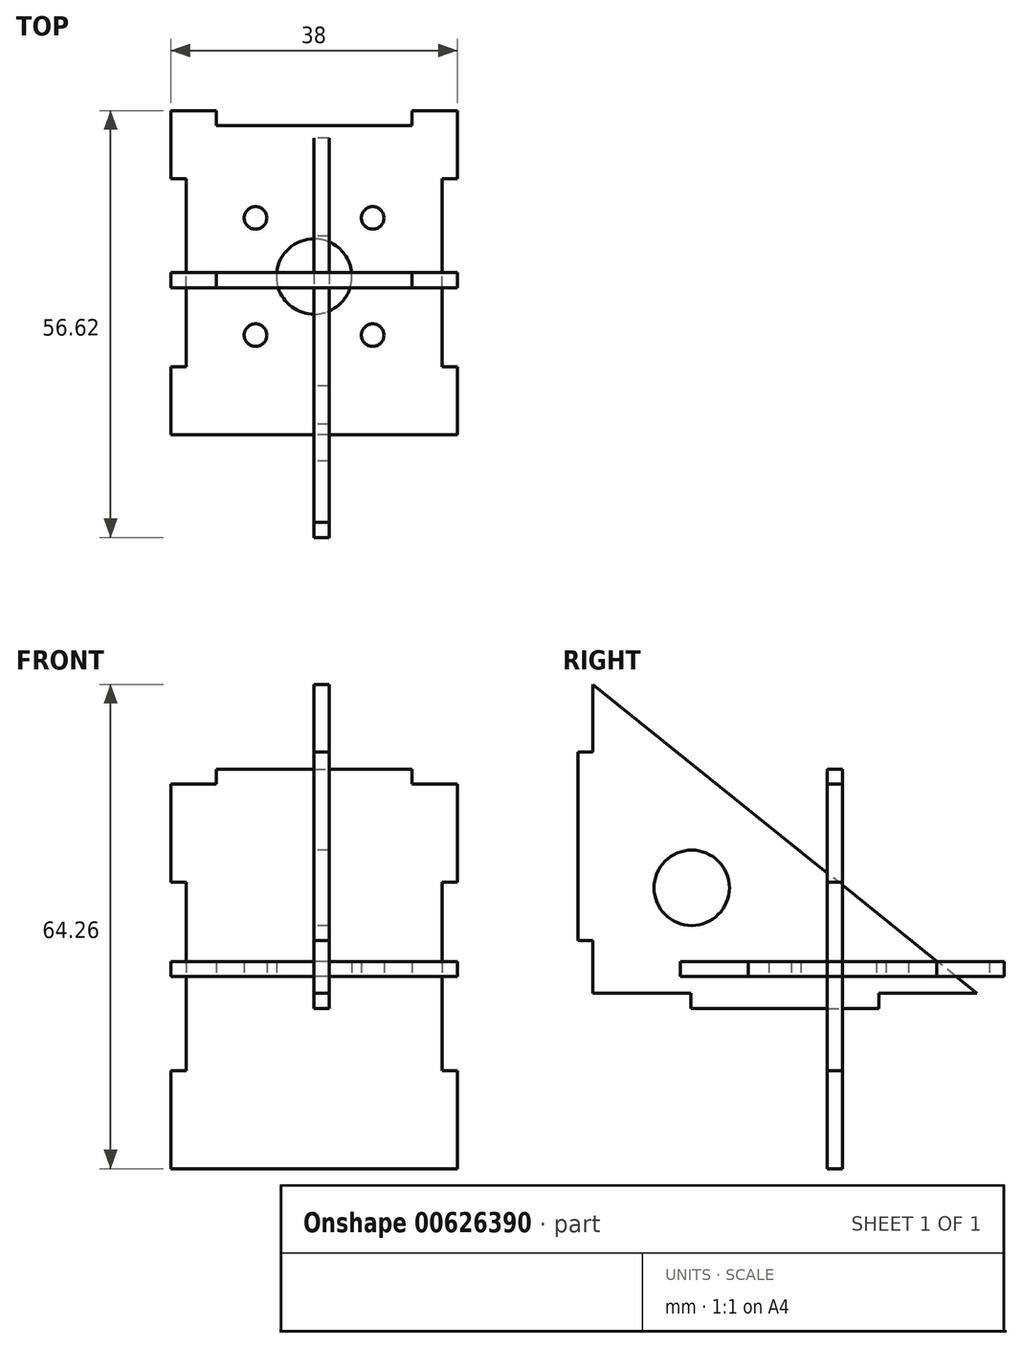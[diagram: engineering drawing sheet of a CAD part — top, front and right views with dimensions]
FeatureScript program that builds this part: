
annotation { "Feature Type Name" : "Feature", "Feature Type Description" : "" }
export const myFeature = defineFeature(function(context is Context, id is Id, definition is map)
    precondition{}
    {
        {
            var Q0;
            Q0=qCreatedBy(makeId("Front.planeOp"),FACE);
            var sketch = newSketch(context, id + "F0", { "sketchPlane" : qUnion([Q0])});
            skLineSegment(sketch, "E0.bottom", {"start": v(19, 25.5) * mm, "end": v(13, 25.5) * mm});
            skLineSegment(sketch, "E0.top", {"start": v(19, -25.5) * mm, "end": v(-19, -25.5) * mm});
            skLineSegment(sketch, "E0.left", {"start": v(19, 25.5) * mm, "end": v(19, 12.5) * mm});
            skLineSegment(sketch, "E0.right", {"start": v(-19, 25.5) * mm, "end": v(-19, 12.5) * mm});
            skPoint(sketch, "E0.middle", {"position": v(0, 0) * mm});
            skLineSegment(sketch, "E1", {"start": v(0, 28.55) * mm, "end": v(0, -30.47) * mm, "construction": true});
            skLineSegment(sketch, "E2.top", {"start": v(-13, 27.5) * mm, "end": v(13, 27.5) * mm});
            skLineSegment(sketch, "E2.left", {"start": v(-13, 25.5) * mm, "end": v(-13, 27.5) * mm});
            skLineSegment(sketch, "E2.right", {"start": v(13, 25.5) * mm, "end": v(13, 27.5) * mm});
            skLineSegment(sketch, "E3.bottom", {"start": v(-19, 12.5) * mm, "end": v(-17, 12.5) * mm});
            skLineSegment(sketch, "E3.top", {"start": v(-19, -12.5) * mm, "end": v(-17, -12.5) * mm});
            skLineSegment(sketch, "E3.right", {"start": v(-17, 12.5) * mm, "end": v(-17, -12.5) * mm});
            skLineSegment(sketch, "E4.MirrorCS", {"start": v(19, 12.5) * mm, "end": v(17, 12.5) * mm});
            skLineSegment(sketch, "E5.MirrorCS", {"start": v(17, 12.5) * mm, "end": v(17, -12.5) * mm});
            skLineSegment(sketch, "E6.MirrorCS", {"start": v(19, -12.5) * mm, "end": v(17, -12.5) * mm});
            skLineSegment(sketch, "E7.trimOffspring", {"start": v(-13, 25.5) * mm, "end": v(-19, 25.5) * mm});
            skLineSegment(sketch, "E8.trimOffspring", {"start": v(-19, -12.5) * mm, "end": v(-19, -25.5) * mm});
            skLineSegment(sketch, "E9.trimOffspring", {"start": v(19, -12.5) * mm, "end": v(19, -25.5) * mm});
            skSolve(sketch);
        }
        {
            var Q0;
            Q0=makeQuery(id+"F0.imprint","IMPRINT",FACE,{"disambiguationData":[TD([[makeQuery(id+"F0.imprint","IMPRINT",EDGE,{"derivedFrom":sQuery(id+"F0.wireOp",EDGE,"E0.bottom")}),1.0]])]});
            extrude(context, id + "F1", {"entities" : qUnion([Q0]), "depth" : 2 * mm, "offsetDistance" : 25 * mm});
        }
        {
            var Q0;
            Q0=makeQuery(id+"F1.opExtrude","SWEPT_BODY",BODY,{"disambiguationData":[OSD([sQuery(id+"F0.wireOp",EDGE,"E0.bottom"),sQuery(id+"F0.wireOp",EDGE,"E0.top"),sQuery(id+"F0.wireOp",EDGE,"E0.left"),sQuery(id+"F0.wireOp",EDGE,"E0.right"),sQuery(id+"F0.wireOp",EDGE,"E2.top"),sQuery(id+"F0.wireOp",EDGE,"E2.left"),sQuery(id+"F0.wireOp",EDGE,"E2.right"),sQuery(id+"F0.wireOp",EDGE,"E3.bottom"),sQuery(id+"F0.wireOp",EDGE,"E3.top"),sQuery(id+"F0.wireOp",EDGE,"E3.right"),sQuery(id+"F0.wireOp",EDGE,"E4.MirrorCS"),sQuery(id+"F0.wireOp",EDGE,"E5.MirrorCS"),sQuery(id+"F0.wireOp",EDGE,"E6.MirrorCS"),sQuery(id+"F0.wireOp",EDGE,"E7.trimOffspring"),sQuery(id+"F0.wireOp",EDGE,"E8.trimOffspring"),sQuery(id+"F0.wireOp",EDGE,"E9.trimOffspring")])]});
            transform(context, id + "F2", {"entities" : qUnion([Q0]), "transformType" : TransformType.TRANSLATION_3D, "dx" : 0 * mm, "dy" : 0 * mm, "dz" : 0 * mm, "makeCopy" : true});
        }
        {
            var Q0;
            Q0=makeQuery(id+"F2.opPattern","COPY",BODY,{"derivedFrom":makeQuery(id+"F1.opExtrude","SWEPT_BODY",BODY,{"disambiguationData":[OSD([sQuery(id+"F0.wireOp",EDGE,"E0.bottom"),sQuery(id+"F0.wireOp",EDGE,"E0.top"),sQuery(id+"F0.wireOp",EDGE,"E0.left"),sQuery(id+"F0.wireOp",EDGE,"E0.right"),sQuery(id+"F0.wireOp",EDGE,"E2.top"),sQuery(id+"F0.wireOp",EDGE,"E2.left"),sQuery(id+"F0.wireOp",EDGE,"E2.right"),sQuery(id+"F0.wireOp",EDGE,"E3.bottom"),sQuery(id+"F0.wireOp",EDGE,"E3.top"),sQuery(id+"F0.wireOp",EDGE,"E3.right"),sQuery(id+"F0.wireOp",EDGE,"E4.MirrorCS"),sQuery(id+"F0.wireOp",EDGE,"E5.MirrorCS"),sQuery(id+"F0.wireOp",EDGE,"E6.MirrorCS"),sQuery(id+"F0.wireOp",EDGE,"E7.trimOffspring"),sQuery(id+"F0.wireOp",EDGE,"E8.trimOffspring"),sQuery(id+"F0.wireOp",EDGE,"E9.trimOffspring")])]}),"instanceName":"1"});
            deleteBodies(context, id + "F3", {"entities" : qUnion([Q0])});
        }
        {
            var Q0;
            Q0=makeQuery(id+"F1.opExtrude","SWEPT_BODY",BODY,{"disambiguationData":[OSD([sQuery(id+"F0.wireOp",EDGE,"E0.bottom"),sQuery(id+"F0.wireOp",EDGE,"E0.top"),sQuery(id+"F0.wireOp",EDGE,"E0.left"),sQuery(id+"F0.wireOp",EDGE,"E0.right"),sQuery(id+"F0.wireOp",EDGE,"E2.top"),sQuery(id+"F0.wireOp",EDGE,"E2.left"),sQuery(id+"F0.wireOp",EDGE,"E2.right"),sQuery(id+"F0.wireOp",EDGE,"E3.bottom"),sQuery(id+"F0.wireOp",EDGE,"E3.top"),sQuery(id+"F0.wireOp",EDGE,"E3.right"),sQuery(id+"F0.wireOp",EDGE,"E4.MirrorCS"),sQuery(id+"F0.wireOp",EDGE,"E5.MirrorCS"),sQuery(id+"F0.wireOp",EDGE,"E6.MirrorCS"),sQuery(id+"F0.wireOp",EDGE,"E7.trimOffspring"),sQuery(id+"F0.wireOp",EDGE,"E8.trimOffspring"),sQuery(id+"F0.wireOp",EDGE,"E9.trimOffspring")])]});
            transform(context, id + "F4", {"entities" : qUnion([Q0]), "transformType" : TransformType.TRANSLATION_3D, "dx" : 0 * mm, "dy" : 0 * mm, "dz" : 0 * mm, "makeCopy" : true});
        }
        {
            var Q0;
            Q0=makeQuery(id+"F4.opPattern","COPY",BODY,{"derivedFrom":makeQuery(id+"F1.opExtrude","SWEPT_BODY",BODY,{"disambiguationData":[OSD([sQuery(id+"F0.wireOp",EDGE,"E0.bottom"),sQuery(id+"F0.wireOp",EDGE,"E0.top"),sQuery(id+"F0.wireOp",EDGE,"E0.left"),sQuery(id+"F0.wireOp",EDGE,"E0.right"),sQuery(id+"F0.wireOp",EDGE,"E2.top"),sQuery(id+"F0.wireOp",EDGE,"E2.left"),sQuery(id+"F0.wireOp",EDGE,"E2.right"),sQuery(id+"F0.wireOp",EDGE,"E3.bottom"),sQuery(id+"F0.wireOp",EDGE,"E3.top"),sQuery(id+"F0.wireOp",EDGE,"E3.right"),sQuery(id+"F0.wireOp",EDGE,"E4.MirrorCS"),sQuery(id+"F0.wireOp",EDGE,"E5.MirrorCS"),sQuery(id+"F0.wireOp",EDGE,"E6.MirrorCS"),sQuery(id+"F0.wireOp",EDGE,"E7.trimOffspring"),sQuery(id+"F0.wireOp",EDGE,"E8.trimOffspring"),sQuery(id+"F0.wireOp",EDGE,"E9.trimOffspring")])]}),"instanceName":"1"});
            deleteBodies(context, id + "F5", {"entities" : qUnion([Q0])});
        }
        {
            var Q0;
            Q0=qCreatedBy(makeId("Top.planeOp"),FACE);
            var sketch = newSketch(context, id + "F6", { "sketchPlane" : qUnion([Q0])});
            skLineSegment(sketch, "E10.bottom", {"start": v(19, 21.5) * mm, "end": v(13, 21.5) * mm});
            skLineSegment(sketch, "E10.top", {"start": v(19, -21.5) * mm, "end": v(-19, -21.5) * mm});
            skLineSegment(sketch, "E10.left", {"start": v(19, 21.5) * mm, "end": v(19, 12.5) * mm});
            skLineSegment(sketch, "E10.right", {"start": v(-19, 21.5) * mm, "end": v(-19, 12.5) * mm});
            skPoint(sketch, "E10.middle", {"position": v(0, 0) * mm});
            skLineSegment(sketch, "E11", {"start": v(0, 40.44) * mm, "end": v(0, -36.26) * mm, "construction": true});
            skPoint(sketch, "E11.endSnap0", {"position": v(0, 21.5) * mm});
            skLineSegment(sketch, "E12", {"start": v(-13, 21.5) * mm, "end": v(-13, 19.5) * mm});
            skLineSegment(sketch, "E13", {"start": v(-13, 19.5) * mm, "end": v(13, 19.5) * mm});
            skLineSegment(sketch, "E14", {"start": v(13, 19.5) * mm, "end": v(13, 21.5) * mm});
            skLineSegment(sketch, "E15", {"start": v(-19, 12.5) * mm, "end": v(-17, 12.5) * mm});
            skLineSegment(sketch, "E16", {"start": v(-17, -12.5) * mm, "end": v(-17, 12.5) * mm});
            skLineSegment(sketch, "E17", {"start": v(-17, -12.5) * mm, "end": v(-19, -12.5) * mm});
            skLineSegment(sketch, "E18.MirrorCS", {"start": v(19, 12.5) * mm, "end": v(17, 12.5) * mm});
            skLineSegment(sketch, "E19.MirrorCS", {"start": v(17, -12.5) * mm, "end": v(17, 12.5) * mm});
            skLineSegment(sketch, "E20.MirrorCS", {"start": v(17, -12.5) * mm, "end": v(19, -12.5) * mm});
            skLineSegment(sketch, "E21.trimOffspring", {"start": v(-13, 21.5) * mm, "end": v(-19, 21.5) * mm});
            skLineSegment(sketch, "E22.trimOffspring", {"start": v(-19, -12.5) * mm, "end": v(-19, -21.5) * mm});
            skLineSegment(sketch, "E23.trimOffspring", {"start": v(19, -12.5) * mm, "end": v(19, -21.5) * mm});
            skCircle(sketch, "E24", {"center": v(0, -0.5) * mm, "radius": 5 * mm});
            skCircle(sketch, "E25", {"center": v(0, -0.5) * mm, "radius": 11 * mm, "construction": true});
            skCircle(sketch, "E26", {"center": v(-7.78, -8.28) * mm, "radius": 1.5 * mm});
            skLineSegment(sketch, "E27", {"start": v(-12.39, -0.5) * mm, "end": v(1.13, -0.5) * mm, "construction": true});
            skLineSegment(sketch, "E28", {"start": v(0, -0.5) * mm, "end": v(-9.4, -9.9) * mm, "construction": true});
            skCircle(sketch, "E29.1.0", {"center": v(7.78, -8.28) * mm, "radius": 1.5 * mm});
            skCircle(sketch, "E29.2.0", {"center": v(7.78, 7.28) * mm, "radius": 1.5 * mm});
            skCircle(sketch, "E29.3.0", {"center": v(-7.78, 7.28) * mm, "radius": 1.5 * mm});
            skSolve(sketch);
        }
        {
            var Q0;
            Q0=makeQuery(id+"F6.imprint","IMPRINT",FACE,{"disambiguationData":[TD([[makeQuery(id+"F6.imprint","IMPRINT",EDGE,{"derivedFrom":sQuery(id+"F6.wireOp",EDGE,"E10.bottom")}),1.0]])]});
            extrude(context, id + "F7", {"entities" : qUnion([Q0]), "depth" : 2 * mm, "offsetDistance" : 25 * mm});
        }
        {
            var Q0;
            Q0=qCreatedBy(makeId("Right.planeOp"),FACE);
            var sketch = newSketch(context, id + "F8", { "sketchPlane" : qUnion([Q0])});
            skLineSegment(sketch, "E30", {"start": v(-33.12, 38.76) * mm, "end": v(-33.12, 29.76) * mm});
            skLineSegment(sketch, "E31", {"start": v(-33.12, 29.76) * mm, "end": v(-35.12, 29.76) * mm});
            skLineSegment(sketch, "E32", {"start": v(-35.12, 29.76) * mm, "end": v(-35.12, 4.76) * mm});
            skLineSegment(sketch, "E33", {"start": v(-35.12, 4.76) * mm, "end": v(-33.12, 4.76) * mm});
            skLineSegment(sketch, "E34", {"start": v(-33.12, 4.76) * mm, "end": v(-33.12, -2.24) * mm});
            skLineSegment(sketch, "E35", {"start": v(-33.12, -2.24) * mm, "end": v(-20.12, -2.24) * mm});
            skLineSegment(sketch, "E36", {"start": v(-20.12, -2.24) * mm, "end": v(-20.12, -4.24) * mm});
            skLineSegment(sketch, "E37", {"start": v(-20.12, -4.24) * mm, "end": v(4.88, -4.24) * mm});
            skLineSegment(sketch, "E38", {"start": v(4.88, -4.24) * mm, "end": v(4.88, -2.24) * mm});
            skLineSegment(sketch, "E39", {"start": v(17.88, -2.24) * mm, "end": v(4.88, -2.24) * mm});
            skLineSegment(sketch, "E40", {"start": v(17.88, -2.24) * mm, "end": v(-33.12, 38.76) * mm});
            skCircle(sketch, "E41", {"center": v(-20, 11.76) * mm, "radius": 5 * mm});
            skSolve(sketch);
        }
        {
            var Q0;
            Q0=makeQuery(id+"F8.imprint","IMPRINT",FACE,{"disambiguationData":[TD([[makeQuery(id+"F8.imprint","IMPRINT",EDGE,{"derivedFrom":sQuery(id+"F8.wireOp",EDGE,"E30")}),1.0]])]});
            extrude(context, id + "F9", {"entities" : qUnion([Q0]), "depth" : 2 * mm, "offsetDistance" : 25 * mm});
        }
    });
